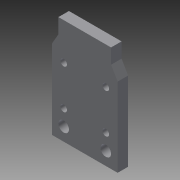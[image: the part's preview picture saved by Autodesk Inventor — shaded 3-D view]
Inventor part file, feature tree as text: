
AUTODESK INVENTOR PART (.ipt)
format: ipt  version: 2013 (Build 170138000, 138)  size: 119,808 bytes
history: native  units: mm
features: sketch x4, extrude x2, hole x2, other x1
ambient origin geometry x8: Origin, YZ Plane, XZ Plane, XY Plane, X Axis, Y Axis, Z Axis, Center Point
feature tree (9):
  other  "ソリッド1"
  extrude  "押し出し1"  Depth=25.0mm
  extrude  "押し出し2"  Depth=40.0mm
  hole  "穴1"  [1 undecoded]
  hole  "穴2"  [1 undecoded]
  sketch  "スケッチ1"
  sketch  "スケッチ2"
  sketch  "スケッチ3"
  sketch  "スケッチ4"
note: 2 required parameter values undecoded (feature->parameter linkage not recoverable at this tier; creation-order binding heuristic only, values carry confidence <= 0.55)
